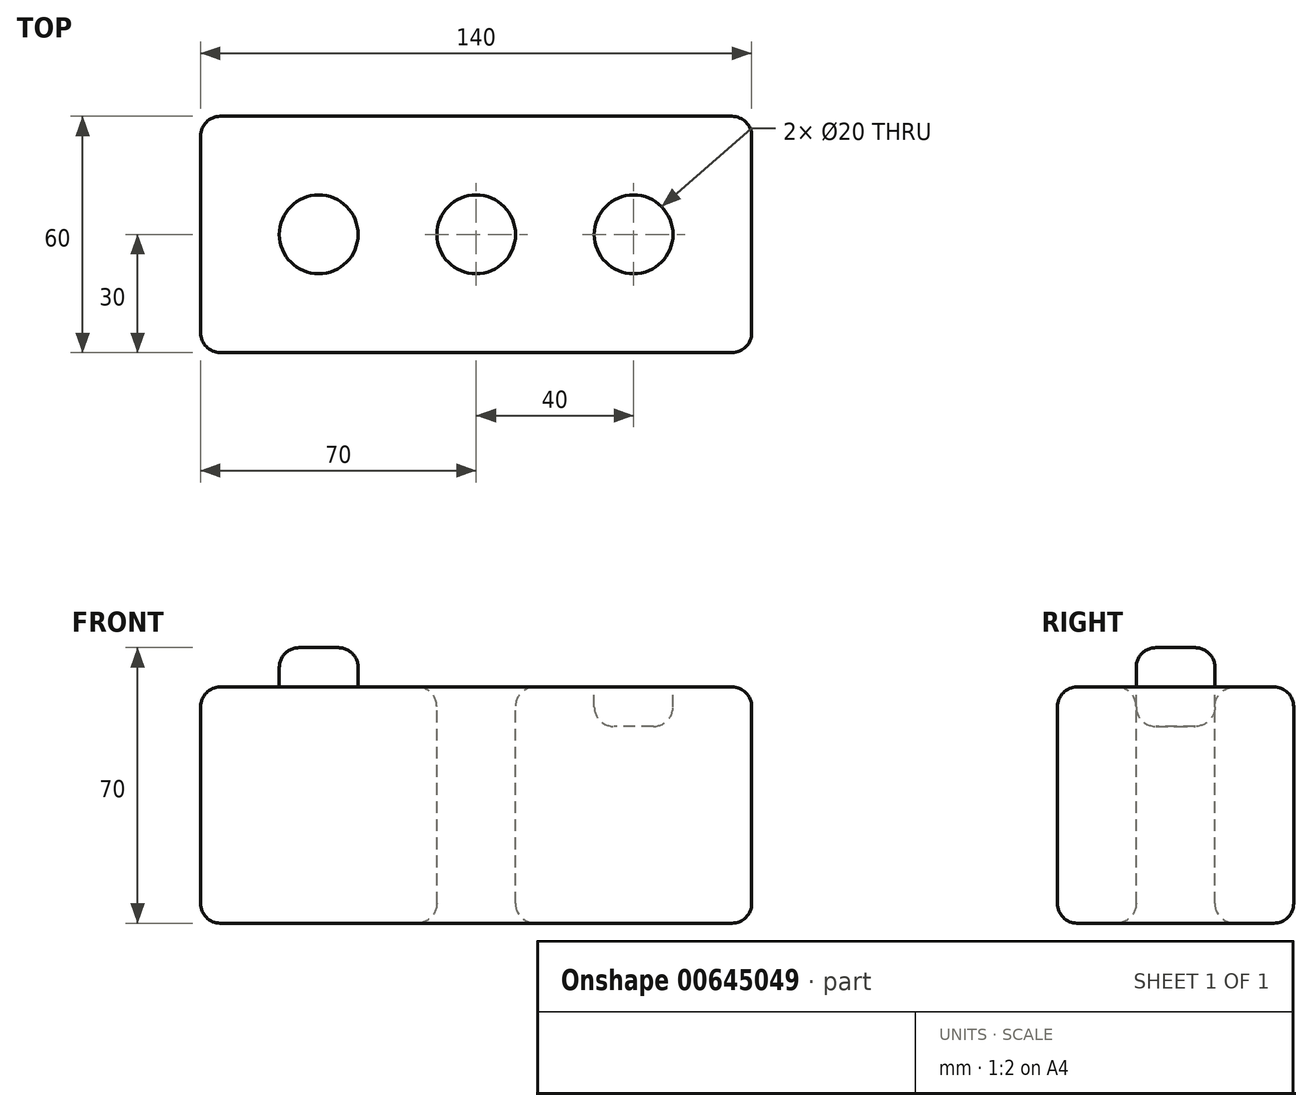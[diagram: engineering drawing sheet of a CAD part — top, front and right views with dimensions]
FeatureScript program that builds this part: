
annotation { "Feature Type Name" : "Feature", "Feature Type Description" : "" }
export const myFeature = defineFeature(function(context is Context, id is Id, definition is map)
    precondition{}
    {
        {
            var Q0;
            Q0=qCreatedBy(makeId("Top.planeOp"),FACE);
            var sketch = newSketch(context, id + "F0", { "sketchPlane" : qUnion([Q0])});
            skLineSegment(sketch, "E0.bottom", {"start": v(-70, 30) * mm, "end": v(70, 30) * mm});
            skLineSegment(sketch, "E0.top", {"start": v(-70, -30) * mm, "end": v(70, -30) * mm});
            skLineSegment(sketch, "E0.left", {"start": v(-70, 30) * mm, "end": v(-70, -30) * mm});
            skLineSegment(sketch, "E0.right", {"start": v(70, 30) * mm, "end": v(70, -30) * mm});
            skPoint(sketch, "E0.middle", {"position": v(0, 0) * mm});
            skSolve(sketch);
        }
        {
            var Q0;
            Q0 = qSketchRegion(id + "F0", true);
            extrude(context, id + "F1", {"entities" : qUnion([Q0]), "depth" : 60 * mm, "offsetDistance" : 25 * mm});
        }
        {
            var Q0;
            Q0=makeQuery(id+"F1.opExtrude","CAP_FACE",FACE,{"disambiguationData":[OSD([sQuery(id+"F0.wireOp",EDGE,"E0.bottom"),sQuery(id+"F0.wireOp",EDGE,"E0.top"),sQuery(id+"F0.wireOp",EDGE,"E0.left"),sQuery(id+"F0.wireOp",EDGE,"E0.right")])],"isStart":false});
            var sketch = newSketch(context, id + "F2", { "sketchPlane" : qUnion([Q0])});
            skCircle(sketch, "E1", {"center": v(-40, 0) * mm, "radius": 10 * mm});
            skSolve(sketch);
        }
        {
            var Q0;
            Q0=makeQuery(id+"F2.imprint","IMPRINT",FACE,{"disambiguationData":[TD([[makeQuery(id+"F2.imprint","IMPRINT",EDGE,{"derivedFrom":sQuery(id+"F2.wireOp",EDGE,"E1")}),-1.0]])]});
            var sketch = newSketch(context, id + "F3", { "sketchPlane" : qUnion([Q0])});
            skCircle(sketch, "E2", {"center": v(40, 0) * mm, "radius": 10 * mm});
            skSolve(sketch);
        }
        {
            var Q0;
            Q0=makeQuery(id+"F2.imprint","IMPRINT",FACE,{"disambiguationData":[TD([[makeQuery(id+"F2.imprint","IMPRINT",EDGE,{"derivedFrom":sQuery(id+"F2.wireOp",EDGE,"E1")}),-1.0]])]});
            var sketch = newSketch(context, id + "F4", { "sketchPlane" : qUnion([Q0])});
            skCircle(sketch, "E3", {"center": v(0, 0) * mm, "radius": 10 * mm});
            skSolve(sketch);
        }
        {
            var Q0;
            Q0 = qSketchRegion(id + "F2", true);
            extrude(context, id + "F5", {"entities" : qUnion([Q0]), "operationType" : NewBodyOperationType.ADD, "depth" : 10 * mm, "offsetDistance" : 25 * mm});
        }
        {
            var Q0;
            Q0 = qSketchRegion(id + "F4", true);
            extrude(context, id + "F6", {"entities" : qUnion([Q0]), "operationType" : NewBodyOperationType.REMOVE, "oppositeDirection" : true, "depth" : 93.7 * mm, "offsetDistance" : 25 * mm});
        }
        {
            var Q0;
            Q0 = qSketchRegion(id + "F3", true);
            extrude(context, id + "F7", {"entities" : qUnion([Q0]), "operationType" : NewBodyOperationType.REMOVE, "oppositeDirection" : true, "depth" : 10 * mm, "offsetDistance" : 25 * mm});
        }
        {
            var Q0;
            Q0=makeQuery(id+"F1.opExtrude","CAP_EDGE",EDGE,{"disambiguationData":[OSD([sQuery(id+"F0.wireOp",EDGE,"E0.bottom")])],"isStart":false});
            var Q1;
            Q1=makeQuery(id+"F1.opExtrude","CAP_EDGE",EDGE,{"disambiguationData":[OSD([sQuery(id+"F0.wireOp",EDGE,"E0.right")])],"isStart":false});
            var Q2;
            Q2=makeQuery(id+"F1.opExtrude","CAP_EDGE",EDGE,{"disambiguationData":[OSD([sQuery(id+"F0.wireOp",EDGE,"E0.top")])],"isStart":false});
            var Q3;
            Q3=makeQuery(id+"F1.opExtrude","CAP_EDGE",EDGE,{"disambiguationData":[OSD([sQuery(id+"F0.wireOp",EDGE,"E0.left")])],"isStart":false});
            var Q4;
            Q4=makeQuery(id+"F1.opExtrude","SWEPT_EDGE",EDGE,{"disambiguationData":[OSD([sQuery(id+"F0.wireOp",EDGE,"E0.top"),sQuery(id+"F0.wireOp",EDGE,"E0.right")])]});
            var Q5;
            Q5=makeQuery(id+"F1.opExtrude","SWEPT_EDGE",EDGE,{"disambiguationData":[OSD([sQuery(id+"F0.wireOp",EDGE,"E0.bottom"),sQuery(id+"F0.wireOp",EDGE,"E0.right")])]});
            var Q6;
            Q6=makeQuery(id+"F1.opExtrude","SWEPT_EDGE",EDGE,{"disambiguationData":[OSD([sQuery(id+"F0.wireOp",EDGE,"E0.top"),sQuery(id+"F0.wireOp",EDGE,"E0.left")])]});
            var Q7;
            Q7=makeQuery(id+"F1.opExtrude","SWEPT_EDGE",EDGE,{"disambiguationData":[OSD([sQuery(id+"F0.wireOp",EDGE,"E0.bottom"),sQuery(id+"F0.wireOp",EDGE,"E0.left")])]});
            var Q8;
            Q8=makeQuery(id+"F5.opExtrude","CAP_EDGE",EDGE,{"disambiguationData":[OSD([sQuery(id+"F2.wireOp",EDGE,"E1")])],"isStart":false});
            var Q9;
            Q9=makeQuery(id+"F6.boolean.opBoolean","COPY",FACE,{"derivedFrom":makeQuery(id+"F6.opExtrude","SWEPT_FACE",FACE,{"disambiguationData":[OSD([sQuery(id+"F4.wireOp",EDGE,"E3")])]})});
            var Q10;
            Q10=makeQuery(id+"F7.boolean.opBoolean","COPY",EDGE,{"derivedFrom":makeQuery(id+"F7.opExtrude","CAP_EDGE",EDGE,{"disambiguationData":[OSD([sQuery(id+"F3.wireOp",EDGE,"E2")])],"isStart":false})});
            var Q11;
            Q11=makeQuery(id+"F5.opExtrude","CAP_EDGE",EDGE,{"disambiguationData":[OSD([sQuery(id+"F2.wireOp",EDGE,"E1")])],"isStart":true});
            var Q12;
            Q12=makeQuery(id+"F1.opExtrude","CAP_EDGE",EDGE,{"disambiguationData":[OSD([sQuery(id+"F0.wireOp",EDGE,"E0.top")])],"isStart":true});
            var Q13;
            Q13=makeQuery(id+"F1.opExtrude","SWEPT_FACE",FACE,{"disambiguationData":[OSD([sQuery(id+"F0.wireOp",EDGE,"E0.right")])]});
            var Q14;
            Q14=makeQuery(id+"F1.opExtrude","CAP_FACE",FACE,{"disambiguationData":[OSD([sQuery(id+"F0.wireOp",EDGE,"E0.bottom"),sQuery(id+"F0.wireOp",EDGE,"E0.top"),sQuery(id+"F0.wireOp",EDGE,"E0.left"),sQuery(id+"F0.wireOp",EDGE,"E0.right")])],"isStart":true});
            var Q15;
            Q15=makeQuery(id+"F1.opExtrude","CAP_EDGE",EDGE,{"disambiguationData":[OSD([sQuery(id+"F0.wireOp",EDGE,"E0.left")])],"isStart":true});
            fillet(context, id + "F8", {"entities" : qUnion([Q0, Q1, Q2, Q3, Q4, Q5, Q6, Q7, Q8, Q9, Q10, Q11, Q12, Q13, Q14, Q15]), "radius" : 5 * mm, "tangentPropagation" : true, "allowEdgeOverflow" : false});
        }
    });
